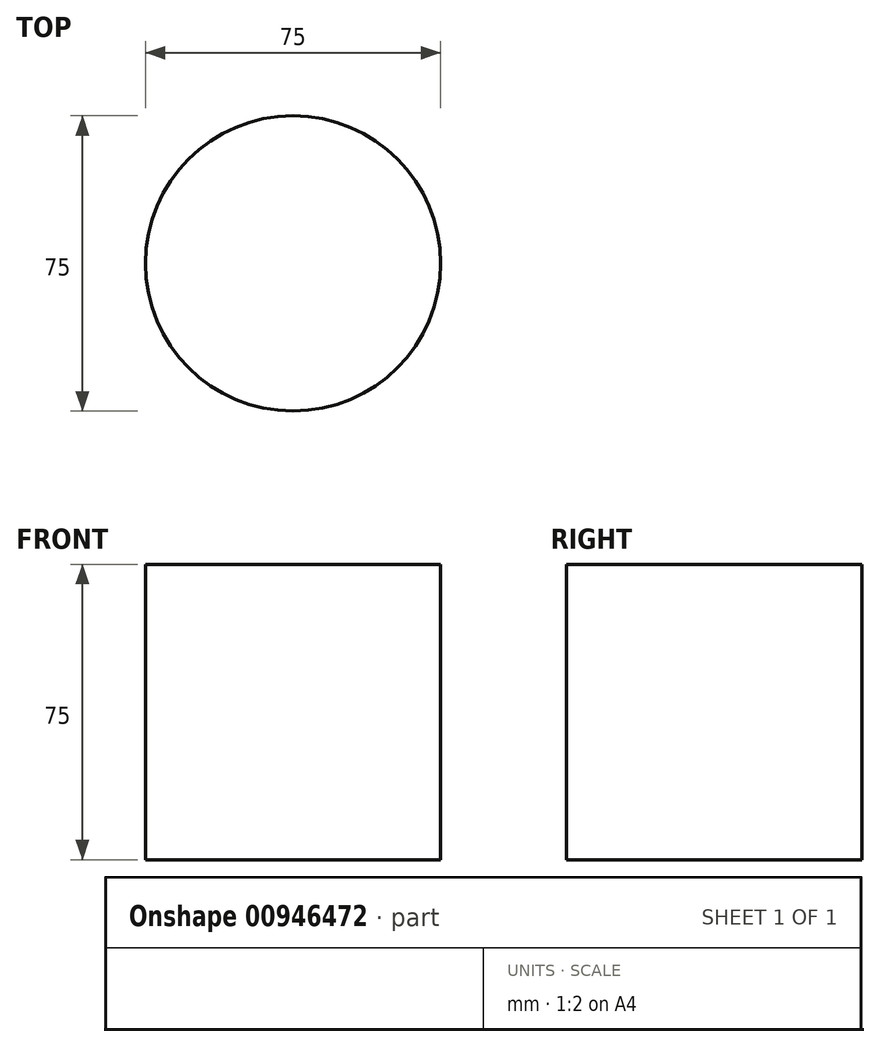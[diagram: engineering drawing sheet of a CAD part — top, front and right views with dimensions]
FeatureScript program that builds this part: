
annotation { "Feature Type Name" : "Feature", "Feature Type Description" : "" }
export const myFeature = defineFeature(function(context is Context, id is Id, definition is map)
    precondition{}
    {
        {
            var Q0;
            Q0=qCreatedBy(makeId("Top.planeOp"),FACE);
            var sketch = newSketch(context, id + "F0", { "sketchPlane" : qUnion([Q0])});
            skCircle(sketch, "E0", {"center": v(0, 0) * mm, "radius": 22.61 * mm});
            skCircle(sketch, "E1", {"center": v(0, 0) * mm, "radius": 37.5 * mm});
            skSolve(sketch);
        }
        {
            var Q0;
            Q0=makeQuery(id+"F0.imprint","IMPRINT",FACE,{"disambiguationData":[TD([[makeQuery(id+"F0.imprint","IMPRINT",EDGE,{"derivedFrom":sQuery(id+"F0.wireOp",EDGE,"E0")}),-1.0]])]});
            var Q1;
            Q1=makeQuery(id+"F0.imprint","IMPRINT",FACE,{"disambiguationData":[TD([[makeQuery(id+"F0.imprint","IMPRINT",EDGE,{"derivedFrom":sQuery(id+"F0.wireOp",EDGE,"E0")}),1.0]])]});
            extrude(context, id + "F1", {"entities" : qUnion([Q0, Q1]), "depth" : 25 * mm, "offsetDistance" : 25 * mm});
        }
        {
            var Q0;
            Q0=makeQuery(id+"F1.opExtrude","CAP_FACE",FACE,{"disambiguationData":[OSD([sQuery(id+"F0.wireOp",EDGE,"E1")])],"isStart":false});
            extrude(context, id + "F2", {"entities" : qUnion([Q0]), "operationType" : NewBodyOperationType.ADD, "depth" : 50 * mm, "offsetDistance" : 25 * mm});
        }
    });
